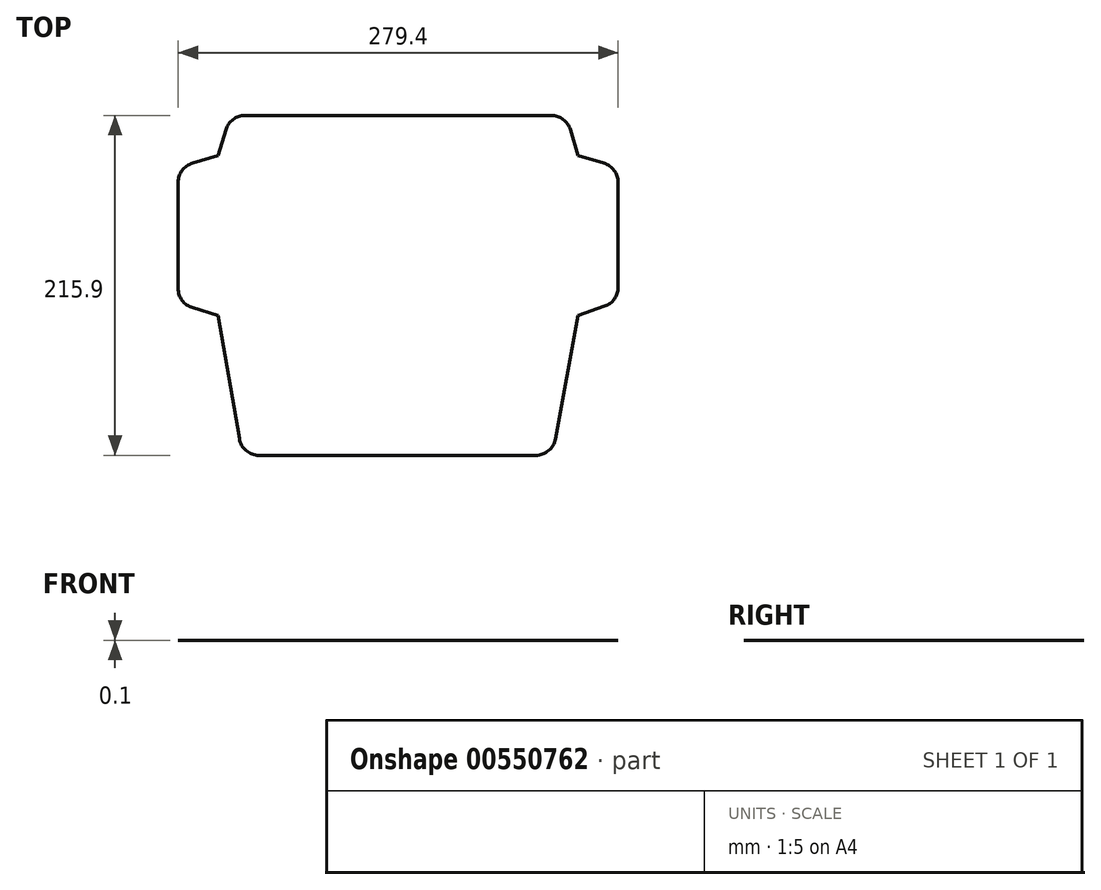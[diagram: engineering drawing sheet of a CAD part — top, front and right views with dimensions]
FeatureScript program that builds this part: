
annotation { "Feature Type Name" : "Feature", "Feature Type Description" : "" }
export const myFeature = defineFeature(function(context is Context, id is Id, definition is map)
    precondition{}
    {
        {
            var Q0;
            Q0=qCreatedBy(makeId("Top.planeOp"),FACE);
            var sketch = newSketch(context, id + "F0", { "sketchPlane" : qUnion([Q0])});
            skLineSegment(sketch, "E0.bottom", {"start": v(0, 215.9) * mm, "end": v(279.4, 215.9) * mm, "construction": true});
            skLineSegment(sketch, "E0.top", {"start": v(0, 0) * mm, "end": v(279.4, 0) * mm, "construction": true});
            skLineSegment(sketch, "E0.left", {"start": v(0, 215.9) * mm, "end": v(0, 0) * mm, "construction": true});
            skLineSegment(sketch, "E0.right", {"start": v(279.4, 215.9) * mm, "end": v(279.4, 0) * mm, "construction": true});
            skLineSegment(sketch, "E1", {"start": v(0, 88.9) * mm, "end": v(279.4, 88.9) * mm, "construction": true});
            skLineSegment(sketch, "E2", {"start": v(0, 190.5) * mm, "end": v(279.4, 190.5) * mm, "construction": true});
            skLineSegment(sketch, "E3", {"start": v(25.4, 215.9) * mm, "end": v(25.4, 0) * mm, "construction": true});
            skLineSegment(sketch, "E4", {"start": v(254, 215.9) * mm, "end": v(254, 0) * mm, "construction": true});
            skLineSegment(sketch, "E5", {"start": v(25.4, 190.5) * mm, "end": v(30.3, 206.85) * mm});
            skLineSegment(sketch, "E6", {"start": v(42.47, 215.9) * mm, "end": v(236.93, 215.9) * mm});
            skLineSegment(sketch, "E7", {"start": v(249.1, 206.85) * mm, "end": v(254, 190.5) * mm});
            skLineSegment(sketch, "E8", {"start": v(254, 190.5) * mm, "end": v(270.35, 185.6) * mm});
            skLineSegment(sketch, "E9", {"start": v(279.4, 173.43) * mm, "end": v(279.4, 106.7) * mm});
            skLineSegment(sketch, "E10", {"start": v(227.1, 0) * mm, "end": v(51.35, 0) * mm});
            skLineSegment(sketch, "E11", {"start": v(38.83, 10.55) * mm, "end": v(25.4, 88.9) * mm});
            skLineSegment(sketch, "E12", {"start": v(25.4, 88.9) * mm, "end": v(9.05, 93.8) * mm});
            skLineSegment(sketch, "E13", {"start": v(0, 105.97) * mm, "end": v(0, 173.43) * mm});
            skLineSegment(sketch, "E14", {"start": v(9.05, 185.6) * mm, "end": v(25.4, 190.5) * mm});
            skLineSegment(sketch, "E15", {"start": v(139.7, 215.9) * mm, "end": v(139.7, 0) * mm, "construction": true});
            skPoint(sketch, "E16.visualSharp", {"position": v(33.02, 215.9) * mm});
            skArc(sketch, "E16.filletArc", {"start": v(42.47, 215.9) * mm, "mid": v(34.89, 213.39) * mm, "end": v(30.3, 206.85) * mm});
            skPoint(sketch, "E17.visualSharp", {"position": v(246.38, 215.9) * mm});
            skArc(sketch, "E17.filletArc", {"start": v(249.1, 206.85) * mm, "mid": v(244.51, 213.39) * mm, "end": v(236.93, 215.9) * mm});
            skPoint(sketch, "E18.visualSharp", {"position": v(0, 182.88) * mm});
            skArc(sketch, "E18.filletArc", {"start": v(9.05, 185.6) * mm, "mid": v(2.51, 181.01) * mm, "end": v(0, 173.43) * mm});
            skPoint(sketch, "E19.visualSharp", {"position": v(0, 96.52) * mm});
            skArc(sketch, "E19.filletArc", {"start": v(0, 105.97) * mm, "mid": v(2.51, 98.39) * mm, "end": v(9.05, 93.8) * mm});
            skPoint(sketch, "E20.visualSharp", {"position": v(279.4, 182.88) * mm});
            skArc(sketch, "E20.filletArc", {"start": v(279.4, 173.43) * mm, "mid": v(276.89, 181.01) * mm, "end": v(270.35, 185.6) * mm});
            skPoint(sketch, "E21.visualSharp", {"position": v(279.4, 96.52) * mm});
            skArc(sketch, "E21.filletArc", {"start": v(270.83, 94.69) * mm, "mid": v(277.04, 99.32) * mm, "end": v(279.4, 106.7) * mm});
            skPoint(sketch, "E22.visualSharp", {"position": v(238.76, 0) * mm});
            skArc(sketch, "E22.filletArc", {"start": v(227.1, 0) * mm, "mid": v(235.23, 2.94) * mm, "end": v(239.6, 10.4) * mm});
            skPoint(sketch, "E23.visualSharp", {"position": v(40.64, 0) * mm});
            skArc(sketch, "E23.filletArc", {"start": v(38.83, 10.55) * mm, "mid": v(43.16, 3) * mm, "end": v(51.35, 0) * mm});
            skLineSegment(sketch, "E24", {"start": v(270.83, 94.69) * mm, "end": v(254, 88.9) * mm});
            skLineSegment(sketch, "E25", {"start": v(254, 88.9) * mm, "end": v(239.6, 10.4) * mm});
            skSolve(sketch);
        }
        {
            var Q0;
            Q0=makeQuery(id+"F0.imprint","IMPRINT",FACE,{"disambiguationData":[TD([[makeQuery(id+"F0.imprint","IMPRINT",EDGE,{"derivedFrom":sQuery(id+"F0.wireOp",EDGE,"E5")}),-1.0]])]});
            extrude(context, id + "F1", {"entities" : qUnion([Q0]), "depth" : 0.1 * mm, "offsetDistance" : 25.4 * mm});
        }
    });
